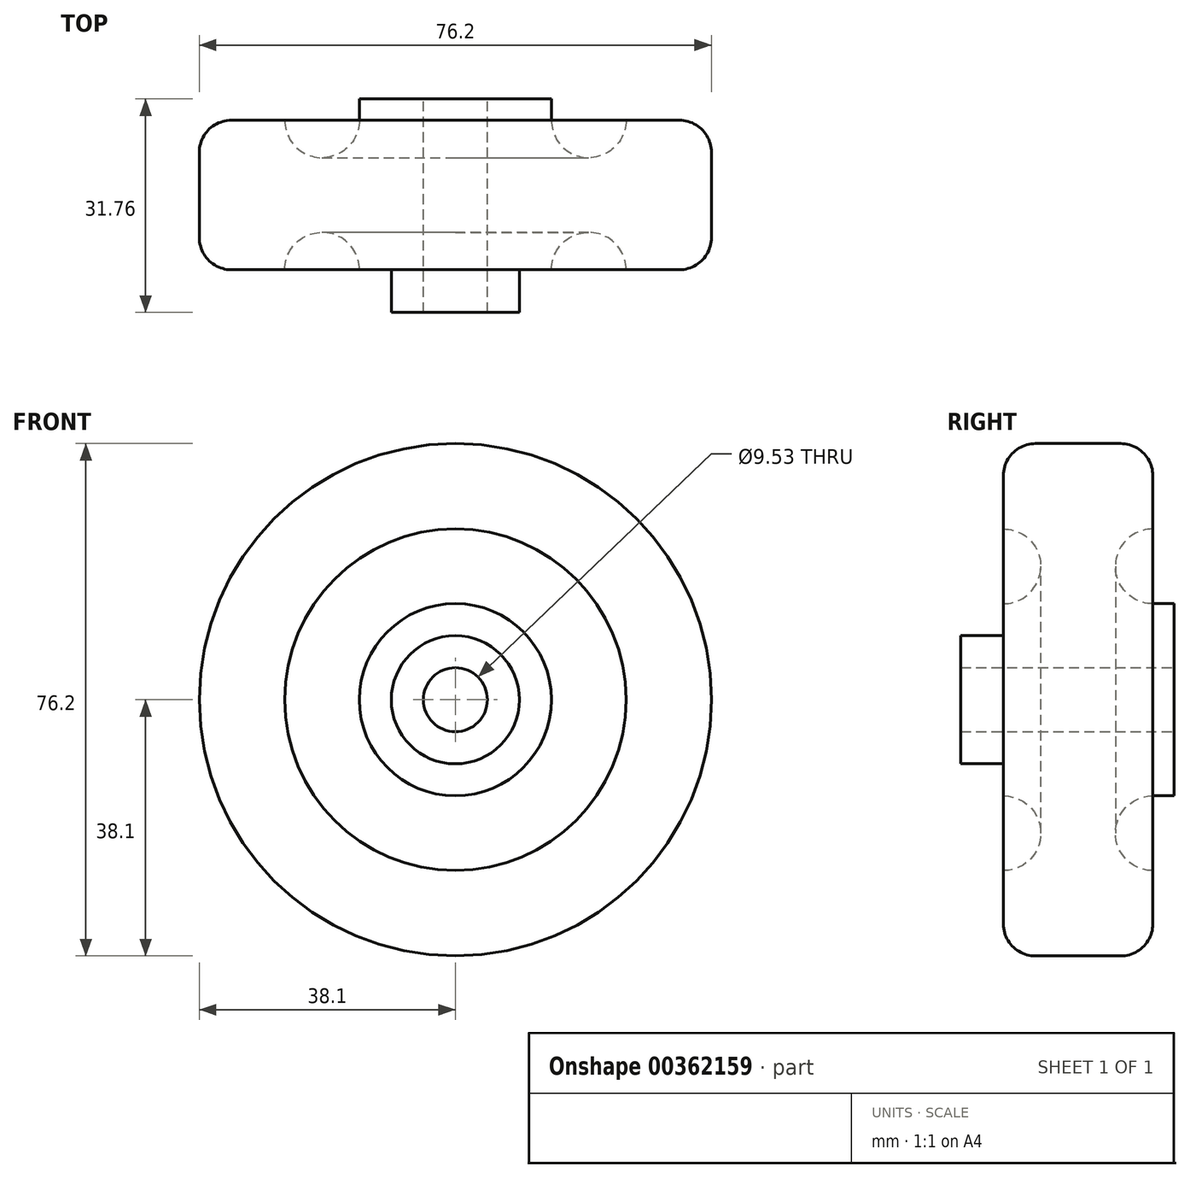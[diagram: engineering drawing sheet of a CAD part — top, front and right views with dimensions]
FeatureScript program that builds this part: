
annotation { "Feature Type Name" : "Feature", "Feature Type Description" : "" }
export const myFeature = defineFeature(function(context is Context, id is Id, definition is map)
    precondition{}
    {
        {
            var Q0;
            Q0=qCreatedBy(makeId("Front.planeOp"),FACE);
            var sketch = newSketch(context, id + "F0", { "sketchPlane" : qUnion([Q0])});
            skCircle(sketch, "E0", {"center": v(0, 0) * mm, "radius": 38.1 * mm});
            skSolve(sketch);
        }
        {
            var Q0;
            Q0=makeQuery(id+"F0.imprint","IMPRINT",FACE,{"disambiguationData":[TD([[makeQuery(id+"F0.imprint","IMPRINT",EDGE,{"derivedFrom":sQuery(id+"F0.wireOp",EDGE,"E0")}),1.0]])]});
            extrude(context, id + "F1", {"entities" : qUnion([Q0]), "depth" : 22.22 * mm});
        }
        {
            var Q0;
            Q0=sQuery(id+"F0.wireOp",VERTEX,"E0.center");
            var Q1;
            Q1=makeQuery(id+"F1.opExtrude","SWEPT_BODY",BODY,{"disambiguationData":[OSD([sQuery(id+"F0.wireOp",EDGE,"E0")])]});
            hole(context, id + "F2", {"style" : HoleStyle.SIMPLE, "endStyle" : HoleEndStyle.THROUGH, "oppositeDirection" : true, "holeDiameter" : 9.52 * mm, "isTappedThrough" : true, "tappedDepth" : 12.7 * mm, "tapClearance" : 3, "startFromSketch" : true, "locations" : qUnion([Q0]), "scope" : qUnion([Q1])});
        }
        {
            var Q0;
            Q0=makeQuery(id+"F1.opExtrude","CAP_FACE",FACE,{"disambiguationData":[OSD([sQuery(id+"F0.wireOp",EDGE,"E0")])],"isStart":false});
            var sketch = newSketch(context, id + "F3", { "sketchPlane" : qUnion([Q0])});
            skCircle(sketch, "E1", {"center": v(0, 0) * mm, "radius": 9.53 * mm});
            skSolve(sketch);
        }
        {
            var Q0;
            Q0=makeQuery(id+"F3.imprint","IMPRINT",FACE,{"disambiguationData":[TD([[makeQuery(id+"F3.imprint","IMPRINT",EDGE,{"derivedFrom":sQuery(id+"F3.wireOp",EDGE,"E1")}),1.0]])]});
            extrude(context, id + "F4", {"entities" : qUnion([Q0]), "operationType" : NewBodyOperationType.ADD, "depth" : 6.35 * mm, "offsetDistance" : 25.4 * mm});
        }
        {
            var Q0;
            Q0=makeQuery(id+"F0.imprint","IMPRINT",FACE,{"disambiguationData":[TD([[makeQuery(id+"F0.imprint","IMPRINT",EDGE,{"derivedFrom":sQuery(id+"F0.wireOp",EDGE,"E0")}),1.0]])]});
            var sketch = newSketch(context, id + "F5", { "sketchPlane" : qUnion([Q0])});
            skCircle(sketch, "E2", {"center": v(0, 0) * mm, "radius": 14.29 * mm});
            skCircle(sketch, "E3.0", {"center": v(0, 0) * mm, "radius": 4.76 * mm});
            skSolve(sketch);
        }
        {
            var Q0;
            Q0 = qSketchRegion(id + "F5", true);
            extrude(context, id + "F6", {"entities" : qUnion([Q0]), "operationType" : NewBodyOperationType.ADD, "oppositeDirection" : true, "depth" : 3.17 * mm});
        }
        {
            var Q0;
            Q0=makeQuery(id+"F1.opExtrude","CAP_EDGE",EDGE,{"disambiguationData":[OSD([sQuery(id+"F0.wireOp",EDGE,"E0")])],"isStart":true});
            var Q1;
            Q1=makeQuery(id+"F1.opExtrude","CAP_EDGE",EDGE,{"disambiguationData":[OSD([sQuery(id+"F0.wireOp",EDGE,"E0")])],"isStart":false});
            fillet(context, id + "F7", {"entities" : qUnion([Q0, Q1]), "radius" : 4.76 * mm, "tangentPropagation" : true, "allowEdgeOverflow" : false});
        }
        {
            var Q0;
            Q0=qCreatedBy(makeId("Right.planeOp"),FACE);
            var sketch = newSketch(context, id + "F8", { "sketchPlane" : qUnion([Q0])});
            skLineSegment(sketch, "E4.0", {"start": v(0, -14.29) * mm, "end": v(0, 14.29) * mm, "construction": true});
            skLineSegment(sketch, "E5.0", {"start": v(0, -14.29) * mm, "end": v(0, 14.29) * mm});
            skLineSegment(sketch, "E6.0", {"start": v(0, 33.34) * mm, "end": v(0, -33.34) * mm, "construction": true});
            skCircle(sketch, "E7", {"center": v(0, 19.84) * mm, "radius": 5.56 * mm});
            skPoint(sketch, "E8.0", {"position": v(0, 0) * mm});
            skLineSegment(sketch, "E9.0.0", {"start": v(-22.23, -33.34) * mm, "end": v(-22.23, 33.34) * mm, "construction": true});
            skCircle(sketch, "E10", {"center": v(-22.23, 19.84) * mm, "radius": 5.56 * mm});
            skPoint(sketch, "E11", {"position": v(-22.23, 0) * mm});
            skSolve(sketch);
        }
        {
            var Q0;
            Q0=makeQuery(id+"F8.imprint","IMPRINT",FACE,{"disambiguationData":[TD([[makeQuery(id+"F8.imprint","IMPRINT",EDGE,{"derivedFrom":sQuery(id+"F8.wireOp",EDGE,"E7")}),1.0]])]});
            var Q1;
            Q1=sQuery(id+"F8.wireOp",EDGE,"E7");
            var Q2;
            {var subQ0=sQuery(id+"F2.hole-0.sketch.wireOp",EDGE,"core_line_2");Q2=makeQuery(id+"F6.boolean.opBoolean","MERGE",FACE,{"derivedFrom":[makeQuery(id+"F4.boolean.opBoolean","MERGE",FACE,{"derivedFrom":[makeQuery(id+"F2.hole-0.boolean.opBoolean","COPY",FACE,{"derivedFrom":makeQuery(id+"F2.hole-0.opRevolve","SWEPT_FACE",FACE,{"disambiguationData":[OSD([subQ0])]})}),makeQuery(id+"F4.opExtrude","SWEPT_FACE",FACE,{"disambiguationData":[OSD([sQuery(id+"F0.wireOp",EDGE,"E0"),subQ0])]})]}),makeQuery(id+"F6.opExtrude","SWEPT_FACE",FACE,{"disambiguationData":[OSD([sQuery(id+"F5.wireOp",EDGE,"E3.0")])]})]});}
            revolve(context, id + "F9", {"operationType" : NewBodyOperationType.REMOVE, "entities" : qUnion([Q0]), "surfaceEntities" : qUnion([Q1]), "axis" : qUnion([Q2]), "revolveType" : RevolveType.FULL, "oppositeDirection" : true});
        }
        {
            var Q0;
            Q0=makeQuery(id+"F8.imprint","IMPRINT",FACE,{"disambiguationData":[TD([[makeQuery(id+"F8.imprint","IMPRINT",EDGE,{"derivedFrom":sQuery(id+"F8.wireOp",EDGE,"E10")}),1.0]])]});
            var Q1;
            Q1=sQuery(id+"F8.wireOp",EDGE,"E10");
            var Q2;
            {var subQ0=sQuery(id+"F2.hole-0.sketch.wireOp",EDGE,"core_line_2");Q2=makeQuery(id+"F6.boolean.opBoolean","MERGE",FACE,{"derivedFrom":[makeQuery(id+"F4.boolean.opBoolean","MERGE",FACE,{"derivedFrom":[makeQuery(id+"F2.hole-0.boolean.opBoolean","COPY",FACE,{"derivedFrom":makeQuery(id+"F2.hole-0.opRevolve","SWEPT_FACE",FACE,{"disambiguationData":[OSD([subQ0])]})}),makeQuery(id+"F4.opExtrude","SWEPT_FACE",FACE,{"disambiguationData":[OSD([sQuery(id+"F0.wireOp",EDGE,"E0"),subQ0])]})]}),makeQuery(id+"F6.opExtrude","SWEPT_FACE",FACE,{"disambiguationData":[OSD([sQuery(id+"F5.wireOp",EDGE,"E3.0")])]})]});}
            revolve(context, id + "F10", {"operationType" : NewBodyOperationType.REMOVE, "entities" : qUnion([Q0]), "surfaceEntities" : qUnion([Q1]), "axis" : qUnion([Q2]), "revolveType" : RevolveType.FULL, "oppositeDirection" : true});
        }
    });
